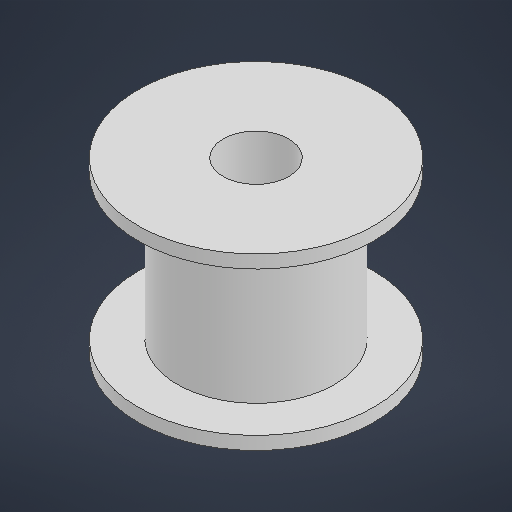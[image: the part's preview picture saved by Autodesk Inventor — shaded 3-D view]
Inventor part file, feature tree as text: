
AUTODESK INVENTOR PART (.ipt)
format: ipt  version: 2025.1 (Build 291241000, 241)  size: 172,032 bytes
history: native  units: mm
features: extrude x3, sketch x1
ambient origin geometry x8: Origin, YZ Plane, XZ Plane, XY Plane, X Axis, Y Axis, Z Axis, Center Point
bodies: Solid1 (feature_tree)
feature tree (4):
  sketch  "Sketch1"  dims[d0=5.0mm d1=18.0mm d2=12.0mm d3=11.0mm d4=0.0mm d5=1.0mm d6=0.0mm d7=1.0mm d8=0.0mm]
  extrude  "Extrusion1"  Depth=1.0mm
  extrude  "Extrusion2"  Depth=12.0mm
  extrude  "Extrusion3"  Depth=11.0mm TaperAngle=0.0deg
